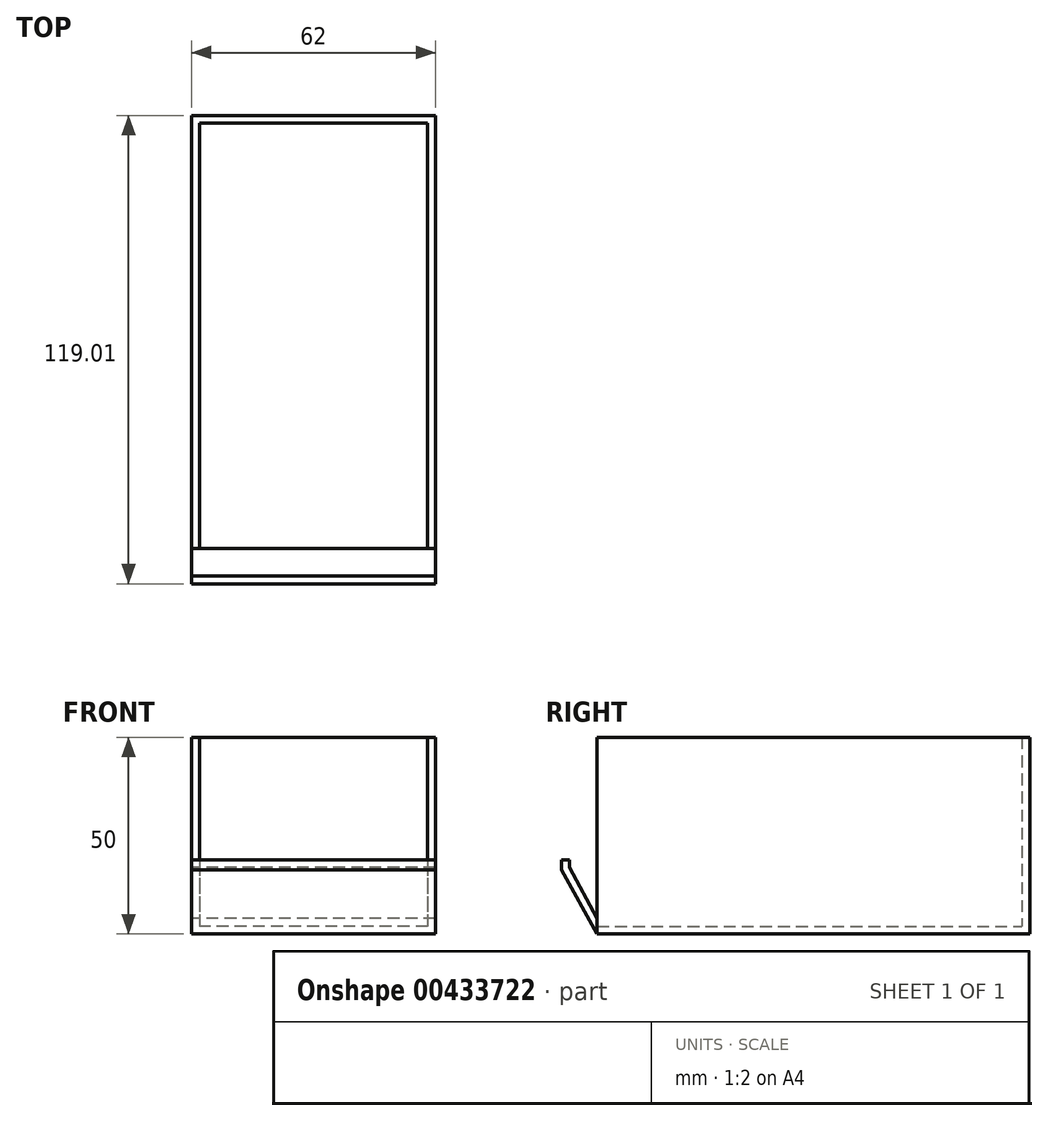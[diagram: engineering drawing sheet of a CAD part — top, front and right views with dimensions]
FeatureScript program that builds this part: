
annotation { "Feature Type Name" : "Feature", "Feature Type Description" : "" }
export const myFeature = defineFeature(function(context is Context, id is Id, definition is map)
    precondition{}
    {
        {
            var Q0;
            Q0=qCreatedBy(makeId("Top.planeOp"),FACE);
            var sketch = newSketch(context, id + "F0", { "sketchPlane" : qUnion([Q0])});
            skLineSegment(sketch, "E0.bottom", {"start": v(31, -55) * mm, "end": v(-31, -55) * mm});
            skLineSegment(sketch, "E0.top", {"start": v(31, 55) * mm, "end": v(-31, 55) * mm});
            skLineSegment(sketch, "E0.left", {"start": v(31, -55) * mm, "end": v(31, 55) * mm});
            skLineSegment(sketch, "E0.right", {"start": v(-31, -55) * mm, "end": v(-31, 55) * mm});
            skPoint(sketch, "E0.middle", {"position": v(0, 0) * mm});
            skSolve(sketch);
        }
        {
            var Q0;
            Q0 = qSketchRegion(id + "F0", true);
            extrude(context, id + "F1", {"entities" : qUnion([Q0]), "depth" : 2 * mm, "offsetDistance" : 25.4 * mm});
        }
        {
            var Q0;
            Q0=qCreatedBy(makeId("Top.planeOp"),FACE);
            var sketch = newSketch(context, id + "F2", { "sketchPlane" : qUnion([Q0])});
            skLineSegment(sketch, "E1.bottom", {"start": v(-31, 55) * mm, "end": v(31, 55) * mm});
            skLineSegment(sketch, "E1.top", {"start": v(-31, 53) * mm, "end": v(31, 53) * mm});
            skLineSegment(sketch, "E1.left", {"start": v(-31, 55) * mm, "end": v(-31, 53) * mm});
            skLineSegment(sketch, "E1.right", {"start": v(31, 55) * mm, "end": v(31, 53) * mm});
            skLineSegment(sketch, "E2.bottom", {"start": v(-31, 55) * mm, "end": v(-29, 55) * mm});
            skLineSegment(sketch, "E2.top", {"start": v(-31, -55) * mm, "end": v(-29, -55) * mm});
            skLineSegment(sketch, "E2.left", {"start": v(-31, 55) * mm, "end": v(-31, -55) * mm});
            skLineSegment(sketch, "E2.right", {"start": v(-29, 55) * mm, "end": v(-29, -55) * mm});
            skLineSegment(sketch, "E3.bottom", {"start": v(31, 55) * mm, "end": v(29, 55) * mm});
            skLineSegment(sketch, "E3.top", {"start": v(31, -55) * mm, "end": v(29, -55) * mm});
            skLineSegment(sketch, "E3.left", {"start": v(31, 55) * mm, "end": v(31, -55) * mm});
            skLineSegment(sketch, "E3.right", {"start": v(29, 55) * mm, "end": v(29, -55) * mm});
            skSolve(sketch);
        }
        {
            var Q0;
            Q0 = qSketchRegion(id + "F2", true);
            extrude(context, id + "F3", {"entities" : qUnion([Q0]), "operationType" : NewBodyOperationType.ADD, "depth" : 50 * mm, "offsetDistance" : 25.4 * mm});
        }
        {
            var Q0;
            Q0=qCreatedBy(makeId("Right.planeOp"),FACE);
            var sketch = newSketch(context, id + "F4", { "sketchPlane" : qUnion([Q0])});
            skLineSegment(sketch, "E4", {"start": v(-55, 0) * mm, "end": v(-64, 16.27) * mm});
            skLineSegment(sketch, "E5", {"start": v(-64, 16.27) * mm, "end": v(-64, 18.83) * mm});
            skLineSegment(sketch, "E6", {"start": v(-64, 18.83) * mm, "end": v(-62, 18.83) * mm});
            skLineSegment(sketch, "E7", {"start": v(-62, 18.83) * mm, "end": v(-62, 16.92) * mm});
            skLineSegment(sketch, "E8", {"start": v(-62, 16.92) * mm, "end": v(-55, 3.97) * mm});
            skLineSegment(sketch, "E9", {"start": v(-55, 3.97) * mm, "end": v(-55, 0) * mm});
            skSolve(sketch);
        }
        {
            var Q0;
            Q0 = qSketchRegion(id + "F4", true);
            extrude(context, id + "F5", {"entities" : qUnion([Q0]), "endBound" : BoundingType.SYMMETRIC, "depth" : 62 * mm, "offsetDistance" : 25.4 * mm});
        }
    });
